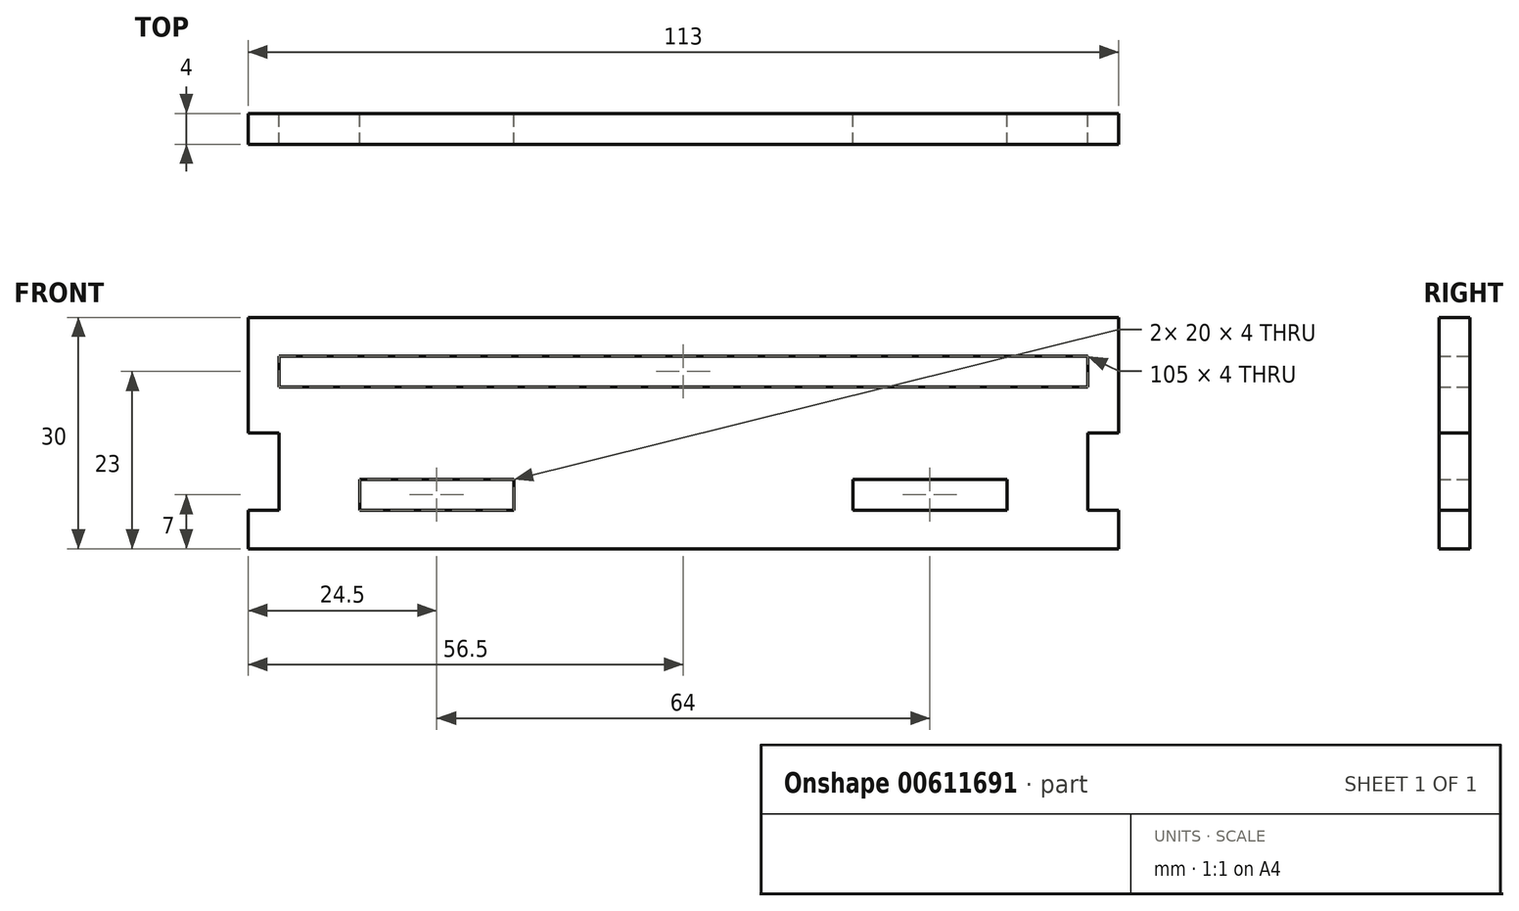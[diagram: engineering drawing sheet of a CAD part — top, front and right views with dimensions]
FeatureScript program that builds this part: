
annotation { "Feature Type Name" : "Feature", "Feature Type Description" : "" }
export const myFeature = defineFeature(function(context is Context, id is Id, definition is map)
    precondition{}
    {
        {
            var Q0;
            Q0=qCreatedBy(makeId("Front.planeOp"),FACE);
            var sketch = newSketch(context, id + "F0", { "sketchPlane" : qUnion([Q0])});
            skLineSegment(sketch, "E0.bottom", {"start": v(56.5, 15) * mm, "end": v(-56.5, 15) * mm});
            skLineSegment(sketch, "E0.top", {"start": v(56.5, -15) * mm, "end": v(-56.5, -15) * mm});
            skLineSegment(sketch, "E0.left", {"start": v(56.5, 15) * mm, "end": v(56.5, 0) * mm});
            skLineSegment(sketch, "E0.right", {"start": v(-56.5, 15) * mm, "end": v(-56.5, 0) * mm});
            skPoint(sketch, "E0.middle", {"position": v(0, 0) * mm});
            skLineSegment(sketch, "E1.bottom", {"start": v(-42, -6) * mm, "end": v(-22, -6) * mm});
            skLineSegment(sketch, "E1.top", {"start": v(-42, -10) * mm, "end": v(-22, -10) * mm});
            skLineSegment(sketch, "E1.left", {"start": v(-42, -6) * mm, "end": v(-42, -10) * mm});
            skLineSegment(sketch, "E1.right", {"start": v(-22, -6) * mm, "end": v(-22, -10) * mm});
            skLineSegment(sketch, "E2.MirrorCS", {"start": v(42, -6) * mm, "end": v(22, -6) * mm});
            skLineSegment(sketch, "E3.MirrorCS", {"start": v(42, -10) * mm, "end": v(22, -10) * mm});
            skLineSegment(sketch, "E4.MirrorCS", {"start": v(42, -6) * mm, "end": v(42, -10) * mm});
            skLineSegment(sketch, "E5.MirrorCS", {"start": v(22, -6) * mm, "end": v(22, -10) * mm});
            skLineSegment(sketch, "E6.bottom", {"start": v(-56.5, 0) * mm, "end": v(-52.5, 0) * mm});
            skLineSegment(sketch, "E6.top", {"start": v(-56.5, -10) * mm, "end": v(-52.5, -10) * mm});
            skLineSegment(sketch, "E6.right", {"start": v(-52.5, 0) * mm, "end": v(-52.5, -10) * mm});
            skLineSegment(sketch, "E7.MirrorCS", {"start": v(56.5, -10) * mm, "end": v(52.5, -10) * mm});
            skLineSegment(sketch, "E8.MirrorCS", {"start": v(52.5, 0) * mm, "end": v(52.5, -10) * mm});
            skLineSegment(sketch, "E9.MirrorCS", {"start": v(56.5, 0) * mm, "end": v(52.5, 0) * mm});
            skLineSegment(sketch, "E10.trimOffspring", {"start": v(-56.5, -10) * mm, "end": v(-56.5, -15) * mm});
            skLineSegment(sketch, "E11.trimOffspring", {"start": v(56.5, -10) * mm, "end": v(56.5, -15) * mm});
            skLineSegment(sketch, "E12.bottom", {"start": v(-52.5, 10) * mm, "end": v(52.5, 10) * mm});
            skLineSegment(sketch, "E12.top", {"start": v(-52.5, 6) * mm, "end": v(52.5, 6) * mm});
            skLineSegment(sketch, "E12.left", {"start": v(-52.5, 10) * mm, "end": v(-52.5, 6) * mm});
            skLineSegment(sketch, "E12.right", {"start": v(52.5, 10) * mm, "end": v(52.5, 6) * mm});
            skSolve(sketch);
        }
        {
            var Q0;
            Q0=makeQuery(id+"F0.imprint","IMPRINT",FACE,{"disambiguationData":[TD([[makeQuery(id+"F0.imprint","IMPRINT",EDGE,{"derivedFrom":sQuery(id+"F0.wireOp",EDGE,"E0.bottom")}),1.0]])]});
            extrude(context, id + "F1", {"entities" : qUnion([Q0]), "depth" : 4 * mm, "offsetDistance" : 25 * mm});
        }
    });
